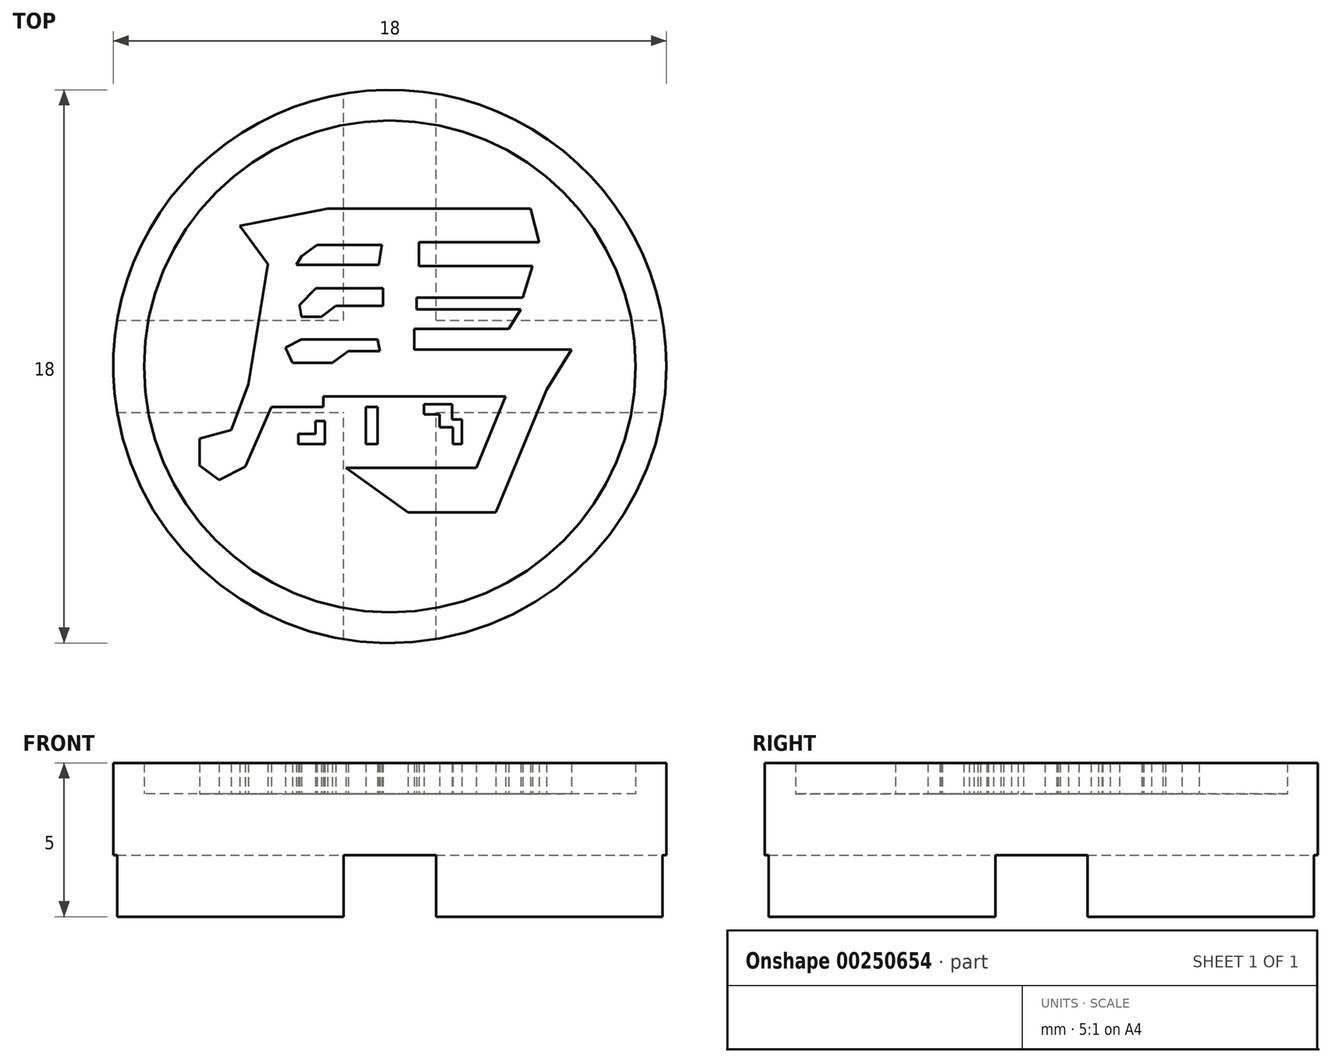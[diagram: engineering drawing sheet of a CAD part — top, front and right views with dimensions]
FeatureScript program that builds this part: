
annotation { "Feature Type Name" : "Feature", "Feature Type Description" : "" }
export const myFeature = defineFeature(function(context is Context, id is Id, definition is map)
    precondition{}
    {
        {
            var Q0;
            Q0=qCreatedBy(makeId("Top.planeOp"),FACE);
            var sketch = newSketch(context, id + "F0", { "sketchPlane" : qUnion([Q0])});
            skCircle(sketch, "E0", {"center": v(-31.33, 19.76) * mm, "radius": 9 * mm});
            skSolve(sketch);
        }
        {
            var Q0;
            Q0=qSketchRegion(id+"F0",true);
            extrude(context, id + "F1", {"entities" : qUnion([Q0]), "depth" : 4 * mm});
        }
        {
            var Q0;
            Q0=makeQuery(id+"F1.opExtrude","CAP_FACE",FACE,{"disambiguationData":[OSD([sQuery(id+"F0.wireOp",EDGE,"E0")])],"isStart":true});
            var sketch = newSketch(context, id + "F2", { "sketchPlane" : qUnion([Q0])});
            skLineSegment(sketch, "E1", {"start": v(-31.33, -19.76) * mm, "end": v(-22.33, -19.76) * mm, "construction": true});
            skLineSegment(sketch, "E2", {"start": v(-31.33, -19.76) * mm, "end": v(-31.33, -10.76) * mm, "construction": true});
            skLineSegment(sketch, "E3", {"start": v(-31.33, -19.76) * mm, "end": v(-40.33, -19.76) * mm, "construction": true});
            skLineSegment(sketch, "E4", {"start": v(-31.33, -19.76) * mm, "end": v(-31.33, -28.76) * mm, "construction": true});
            skLineSegment(sketch, "E5.bottom", {"start": v(-40.33, -28.76) * mm, "end": v(-22.33, -28.76) * mm});
            skLineSegment(sketch, "E5.top", {"start": v(-40.33, -10.76) * mm, "end": v(-22.33, -10.76) * mm});
            skLineSegment(sketch, "E5.left", {"start": v(-22.33, -10.76) * mm, "end": v(-22.33, -28.76) * mm});
            skLineSegment(sketch, "E5.right", {"start": v(-40.33, -10.76) * mm, "end": v(-40.33, -28.76) * mm});
            skPoint(sketch, "E6", {"position": v(-31.33, -28.76) * mm});
            skPoint(sketch, "E7", {"position": v(-40.33, -19.76) * mm});
            skPoint(sketch, "E8", {"position": v(-22.33, -19.76) * mm});
            skPoint(sketch, "E9", {"position": v(-31.33, -10.76) * mm});
            skLineSegment(sketch, "E10.bottom", {"start": v(-32.83, -10.76) * mm, "end": v(-29.83, -10.76) * mm});
            skLineSegment(sketch, "E10.top", {"start": v(-32.83, -28.76) * mm, "end": v(-29.83, -28.76) * mm});
            skLineSegment(sketch, "E10.left", {"start": v(-32.83, -10.76) * mm, "end": v(-32.83, -28.76) * mm});
            skLineSegment(sketch, "E10.right", {"start": v(-29.83, -10.76) * mm, "end": v(-29.83, -28.76) * mm});
            skLineSegment(sketch, "E11.bottom", {"start": v(-40.33, -18.26) * mm, "end": v(-22.33, -18.26) * mm});
            skLineSegment(sketch, "E11.top", {"start": v(-40.33, -21.26) * mm, "end": v(-22.33, -21.26) * mm});
            skLineSegment(sketch, "E11.left", {"start": v(-40.33, -18.26) * mm, "end": v(-40.33, -21.26) * mm});
            skLineSegment(sketch, "E11.right", {"start": v(-22.33, -18.26) * mm, "end": v(-22.33, -21.26) * mm});
            skSolve(sketch);
        }
        {
            var Q0;
            {var subQ1=sQuery(id+"F2.wireOp",EDGE,"E10.bottom");var subQ3=makeQuery(id+"F1.opExtrude","CAP_EDGE",EDGE,{"disambiguationData":[OSD([sQuery(id+"F0.wireOp",EDGE,"E0")])],"isStart":true});var subQ4=makeQuery(id+"F2.imprint","INTERSECT",VERTEX,{"derivedFrom":[subQ3,subQ1]});Q0=makeQuery(id+"F2.imprint","IMPRINT",FACE,{"disambiguationData":[TD([[makeQuery(id+"F2.imprint","IMPRINT",EDGE,{"disambiguationData":[TD([[subQ4,1.0]])],"derivedFrom":subQ3}),1.0]])]});}
            var Q1;
            {var subQ1=sQuery(id+"F2.wireOp",EDGE,"E10.bottom");var subQ3=makeQuery(id+"F1.opExtrude","CAP_EDGE",EDGE,{"disambiguationData":[OSD([sQuery(id+"F0.wireOp",EDGE,"E0")])],"isStart":true});var subQ4=makeQuery(id+"F2.imprint","INTERSECT",VERTEX,{"derivedFrom":[subQ3,subQ1]});Q1=makeQuery(id+"F2.imprint","IMPRINT",FACE,{"disambiguationData":[TD([[makeQuery(id+"F2.imprint","IMPRINT",EDGE,{"disambiguationData":[TD([[subQ4,-1.0]])],"derivedFrom":subQ3}),1.0]])]});}
            var Q2;
            {var subQ1=sQuery(id+"F2.wireOp",EDGE,"E10.top");var subQ3=makeQuery(id+"F1.opExtrude","CAP_EDGE",EDGE,{"disambiguationData":[OSD([sQuery(id+"F0.wireOp",EDGE,"E0")])],"isStart":true});var subQ4=makeQuery(id+"F2.imprint","INTERSECT",VERTEX,{"derivedFrom":[subQ3,subQ1]});Q2=makeQuery(id+"F2.imprint","IMPRINT",FACE,{"disambiguationData":[TD([[makeQuery(id+"F2.imprint","IMPRINT",EDGE,{"disambiguationData":[TD([[subQ4,-1.0]])],"derivedFrom":subQ3}),1.0]])]});}
            var Q3;
            {var subQ1=sQuery(id+"F2.wireOp",EDGE,"E10.top");var subQ3=makeQuery(id+"F1.opExtrude","CAP_EDGE",EDGE,{"disambiguationData":[OSD([sQuery(id+"F0.wireOp",EDGE,"E0")])],"isStart":true});var subQ4=makeQuery(id+"F2.imprint","INTERSECT",VERTEX,{"derivedFrom":[subQ3,subQ1]});Q3=makeQuery(id+"F2.imprint","IMPRINT",FACE,{"disambiguationData":[TD([[makeQuery(id+"F2.imprint","IMPRINT",EDGE,{"disambiguationData":[TD([[subQ4,1.0]])],"derivedFrom":subQ3}),1.0]])]});}
            var Q4;
            {var subQ0=sQuery(id+"F2.wireOp",EDGE,"E11.left");var subQ3=makeQuery(id+"F1.opExtrude","CAP_EDGE",EDGE,{"disambiguationData":[OSD([sQuery(id+"F0.wireOp",EDGE,"E0")])],"isStart":true});var subQ5=makeQuery(id+"F2.imprint","INTERSECT",VERTEX,{"derivedFrom":[subQ3,subQ0]});Q4=makeQuery(id+"F2.imprint","IMPRINT",FACE,{"disambiguationData":[TD([[makeQuery(id+"F2.imprint","IMPRINT",EDGE,{"disambiguationData":[TD([[subQ5,-1.0]])],"derivedFrom":subQ3}),1.0]])]});}
            var Q5;
            {var subQ0=sQuery(id+"F2.wireOp",EDGE,"E11.right");var subQ3=makeQuery(id+"F1.opExtrude","CAP_EDGE",EDGE,{"disambiguationData":[OSD([sQuery(id+"F0.wireOp",EDGE,"E0")])],"isStart":true});var subQ5=makeQuery(id+"F2.imprint","INTERSECT",VERTEX,{"derivedFrom":[subQ3,subQ0]});Q5=makeQuery(id+"F2.imprint","IMPRINT",FACE,{"disambiguationData":[TD([[makeQuery(id+"F2.imprint","IMPRINT",EDGE,{"disambiguationData":[TD([[subQ5,1.0]])],"derivedFrom":subQ3}),1.0]])]});}
            var Q6;
            {var subQ0=sQuery(id+"F2.wireOp",EDGE,"E11.left");var subQ3=makeQuery(id+"F1.opExtrude","CAP_EDGE",EDGE,{"disambiguationData":[OSD([sQuery(id+"F0.wireOp",EDGE,"E0")])],"isStart":true});var subQ5=makeQuery(id+"F2.imprint","INTERSECT",VERTEX,{"derivedFrom":[subQ3,subQ0]});Q6=makeQuery(id+"F2.imprint","IMPRINT",FACE,{"disambiguationData":[TD([[makeQuery(id+"F2.imprint","IMPRINT",EDGE,{"disambiguationData":[TD([[subQ5,1.0]])],"derivedFrom":subQ3}),1.0]])]});}
            var Q7;
            {var subQ0=sQuery(id+"F2.wireOp",EDGE,"E11.right");var subQ3=makeQuery(id+"F1.opExtrude","CAP_EDGE",EDGE,{"disambiguationData":[OSD([sQuery(id+"F0.wireOp",EDGE,"E0")])],"isStart":true});var subQ5=makeQuery(id+"F2.imprint","INTERSECT",VERTEX,{"derivedFrom":[subQ3,subQ0]});Q7=makeQuery(id+"F2.imprint","IMPRINT",FACE,{"disambiguationData":[TD([[makeQuery(id+"F2.imprint","IMPRINT",EDGE,{"disambiguationData":[TD([[subQ5,-1.0]])],"derivedFrom":subQ3}),1.0]])]});}
            var Q8;
            {var subQ3=makeQuery(id+"F1.opExtrude","CAP_EDGE",EDGE,{"disambiguationData":[OSD([sQuery(id+"F0.wireOp",EDGE,"E0")])],"isStart":true});var subQ5=sQuery(id+"F2.wireOp",EDGE,"E10.left");var subQ8=makeQuery(id+"F2.imprint","INTERSECT",VERTEX,{"disambiguationData":[OD(1.0)],"derivedFrom":[subQ3,subQ5]});Q8=makeQuery(id+"F2.imprint","IMPRINT",FACE,{"disambiguationData":[TD([[makeQuery(id+"F2.imprint","IMPRINT",EDGE,{"disambiguationData":[TD([[subQ8,-1.0]])],"derivedFrom":subQ3}),1.0]])]});}
            var Q9;
            {var subQ3=makeQuery(id+"F1.opExtrude","CAP_EDGE",EDGE,{"disambiguationData":[OSD([sQuery(id+"F0.wireOp",EDGE,"E0")])],"isStart":true});var subQ5=sQuery(id+"F2.wireOp",EDGE,"E10.right");var subQ8=makeQuery(id+"F2.imprint","INTERSECT",VERTEX,{"disambiguationData":[OD(1.0)],"derivedFrom":[subQ3,subQ5]});Q9=makeQuery(id+"F2.imprint","IMPRINT",FACE,{"disambiguationData":[TD([[makeQuery(id+"F2.imprint","IMPRINT",EDGE,{"disambiguationData":[TD([[subQ8,1.0]])],"derivedFrom":subQ3}),1.0]])]});}
            var Q10;
            {var subQ3=makeQuery(id+"F1.opExtrude","CAP_EDGE",EDGE,{"disambiguationData":[OSD([sQuery(id+"F0.wireOp",EDGE,"E0")])],"isStart":true});var subQ5=sQuery(id+"F2.wireOp",EDGE,"E10.left");var subQ8=makeQuery(id+"F2.imprint","INTERSECT",VERTEX,{"disambiguationData":[OD(0.0)],"derivedFrom":[subQ3,subQ5]});Q10=makeQuery(id+"F2.imprint","IMPRINT",FACE,{"disambiguationData":[TD([[makeQuery(id+"F2.imprint","IMPRINT",EDGE,{"disambiguationData":[TD([[subQ8,1.0]])],"derivedFrom":subQ3}),1.0]])]});}
            var Q11;
            {var subQ3=makeQuery(id+"F1.opExtrude","CAP_EDGE",EDGE,{"disambiguationData":[OSD([sQuery(id+"F0.wireOp",EDGE,"E0")])],"isStart":true});var subQ5=sQuery(id+"F2.wireOp",EDGE,"E10.right");var subQ8=makeQuery(id+"F2.imprint","INTERSECT",VERTEX,{"disambiguationData":[OD(0.0)],"derivedFrom":[subQ3,subQ5]});Q11=makeQuery(id+"F2.imprint","IMPRINT",FACE,{"disambiguationData":[TD([[makeQuery(id+"F2.imprint","IMPRINT",EDGE,{"disambiguationData":[TD([[subQ8,-1.0]])],"derivedFrom":subQ3}),1.0]])]});}
            var Q12;
            {var subQ2=sQuery(id+"F2.wireOp",EDGE,"E10.left");var subQ4=sQuery(id+"F2.wireOp",EDGE,"E11.bottom");var subQ8=makeQuery(id+"F2.imprint","INTERSECT",VERTEX,{"derivedFrom":[subQ2,subQ4]});Q12=makeQuery(id+"F2.imprint","IMPRINT",FACE,{"disambiguationData":[TD([[makeQuery(id+"F2.imprint","IMPRINT",EDGE,{"disambiguationData":[TD([[subQ8,1.0]])],"derivedFrom":subQ2}),1.0]])]});}
            var Q13;
            {var subQ1=sQuery(id+"F2.wireOp",EDGE,"E10.left");var subQ5=sQuery(id+"F2.wireOp",EDGE,"E11.bottom");var subQ6=makeQuery(id+"F2.imprint","INTERSECT",VERTEX,{"derivedFrom":[subQ1,subQ5]});Q13=makeQuery(id+"F2.imprint","IMPRINT",FACE,{"disambiguationData":[TD([[makeQuery(id+"F2.imprint","IMPRINT",EDGE,{"disambiguationData":[TD([[subQ6,-1.0]])],"derivedFrom":subQ1}),-1.0]])]});}
            var Q14;
            {var subQ0=sQuery(id+"F2.wireOp",EDGE,"E11.top");var subQ1=sQuery(id+"F2.wireOp",EDGE,"E10.left");var subQ2=makeQuery(id+"F2.imprint","INTERSECT",VERTEX,{"derivedFrom":[subQ1,subQ0]});Q14=makeQuery(id+"F2.imprint","IMPRINT",FACE,{"disambiguationData":[TD([[makeQuery(id+"F2.imprint","IMPRINT",EDGE,{"disambiguationData":[TD([[subQ2,-1.0]])],"derivedFrom":subQ1}),1.0]])]});}
            var Q15;
            {var subQ2=sQuery(id+"F2.wireOp",EDGE,"E11.bottom");var subQ5=sQuery(id+"F2.wireOp",EDGE,"E10.right");var subQ8=makeQuery(id+"F2.imprint","INTERSECT",VERTEX,{"derivedFrom":[subQ5,subQ2]});Q15=makeQuery(id+"F2.imprint","IMPRINT",FACE,{"disambiguationData":[TD([[makeQuery(id+"F2.imprint","IMPRINT",EDGE,{"disambiguationData":[TD([[subQ8,-1.0]])],"derivedFrom":subQ5}),1.0]])]});}
            var Q16;
            {var subQ0=sQuery(id+"F2.wireOp",EDGE,"E11.bottom");var subQ1=sQuery(id+"F2.wireOp",EDGE,"E10.left");var subQ2=makeQuery(id+"F2.imprint","INTERSECT",VERTEX,{"derivedFrom":[subQ1,subQ0]});Q16=makeQuery(id+"F2.imprint","IMPRINT",FACE,{"disambiguationData":[TD([[makeQuery(id+"F2.imprint","IMPRINT",EDGE,{"disambiguationData":[TD([[subQ2,-1.0]])],"derivedFrom":subQ1}),1.0]])]});}
            extrude(context, id + "F3", {"entities" : qUnion([Q0, Q1, Q2, Q3, Q4, Q5, Q6, Q7, Q8, Q9, Q10, Q11, Q12, Q13, Q14, Q15, Q16]), "operationType" : NewBodyOperationType.REMOVE, "oppositeDirection" : true, "depth" : 2 * mm});
        }
        {
            var Q0;
            Q0=makeQuery(id+"F1.opExtrude","CAP_FACE",FACE,{"disambiguationData":[OSD([sQuery(id+"F0.wireOp",EDGE,"E0")])],"isStart":false});
            var sketch = newSketch(context, id + "F5", { "sketchPlane" : qUnion([Q0])});
            skCircle(sketch, "E12", {"center": v(-31.33, 19.76) * mm, "radius": 9 * mm});
            skPoint(sketch, "E12.first.point", {"position": v(-33.38, 11) * mm});
            skPoint(sketch, "E12.second.point", {"position": v(-27.6, 27.94) * mm});
            skPoint(sketch, "E12.third.point", {"position": v(-40.33, 19.54) * mm});
            skCircle(sketch, "E13", {"center": v(-31.33, 19.76) * mm, "radius": 8 * mm});
            skLineSegment(sketch, "E14", {"start": v(-36.21, 24.33) * mm, "end": v(-33.35, 24.9) * mm});
            skLineSegment(sketch, "E15", {"start": v(-33.35, 24.9) * mm, "end": v(-26.76, 24.9) * mm});
            skLineSegment(sketch, "E16", {"start": v(-26.76, 24.9) * mm, "end": v(-26.47, 23.8) * mm});
            skLineSegment(sketch, "E17", {"start": v(-26.47, 23.8) * mm, "end": v(-30.4, 23.8) * mm});
            skLineSegment(sketch, "E18", {"start": v(-30.4, 23.8) * mm, "end": v(-30.4, 23.02) * mm});
            skLineSegment(sketch, "E19", {"start": v(-30.4, 23.02) * mm, "end": v(-26.69, 23.02) * mm});
            skLineSegment(sketch, "E20", {"start": v(-26.69, 23.02) * mm, "end": v(-27, 22) * mm});
            skLineSegment(sketch, "E21", {"start": v(-27, 22) * mm, "end": v(-30.46, 22) * mm});
            skLineSegment(sketch, "E22", {"start": v(-30.46, 22) * mm, "end": v(-30.46, 21.61) * mm});
            skLineSegment(sketch, "E23", {"start": v(-30.46, 21.61) * mm, "end": v(-27.07, 21.61) * mm});
            skLineSegment(sketch, "E24", {"start": v(-27.07, 21.61) * mm, "end": v(-27.46, 20.98) * mm});
            skLineSegment(sketch, "E25", {"start": v(-27.46, 20.98) * mm, "end": v(-30.53, 20.98) * mm});
            skLineSegment(sketch, "E26", {"start": v(-30.53, 20.98) * mm, "end": v(-30.53, 20.3) * mm});
            skLineSegment(sketch, "E27", {"start": v(-30.53, 20.3) * mm, "end": v(-25.42, 20.3) * mm});
            skLineSegment(sketch, "E28", {"start": v(-25.42, 20.3) * mm, "end": v(-26.23, 19) * mm});
            skLineSegment(sketch, "E29", {"start": v(-26.23, 19) * mm, "end": v(-27.89, 15.01) * mm});
            skLineSegment(sketch, "E30", {"start": v(-27.89, 15.01) * mm, "end": v(-30.74, 15.01) * mm});
            skLineSegment(sketch, "E31", {"start": v(-30.74, 15.01) * mm, "end": v(-32.75, 16.46) * mm});
            skLineSegment(sketch, "E32", {"start": v(-32.75, 16.46) * mm, "end": v(-28.52, 16.46) * mm});
            skLineSegment(sketch, "E33", {"start": v(-28.52, 16.46) * mm, "end": v(-27.57, 18.79) * mm});
            skLineSegment(sketch, "E34", {"start": v(-27.57, 18.79) * mm, "end": v(-33.5, 18.79) * mm});
            skLineSegment(sketch, "E35", {"start": v(-33.5, 18.79) * mm, "end": v(-33.5, 18.44) * mm});
            skLineSegment(sketch, "E36", {"start": v(-33.5, 18.44) * mm, "end": v(-35.19, 18.44) * mm});
            skLineSegment(sketch, "E37", {"start": v(-35.19, 18.44) * mm, "end": v(-36.04, 16.5) * mm});
            skLineSegment(sketch, "E38", {"start": v(-36.04, 16.5) * mm, "end": v(-36.88, 16.07) * mm});
            skLineSegment(sketch, "E39", {"start": v(-36.88, 16.07) * mm, "end": v(-37.52, 16.53) * mm});
            skLineSegment(sketch, "E40", {"start": v(-37.52, 16.53) * mm, "end": v(-37.52, 17.41) * mm});
            skLineSegment(sketch, "E41", {"start": v(-37.52, 17.41) * mm, "end": v(-36.5, 17.7) * mm});
            skLineSegment(sketch, "E42", {"start": v(-36.5, 17.7) * mm, "end": v(-35.93, 19.18) * mm});
            skLineSegment(sketch, "E43", {"start": v(-35.93, 19.18) * mm, "end": v(-35.3, 23.1) * mm});
            skLineSegment(sketch, "E44", {"start": v(-35.3, 23.1) * mm, "end": v(-36.21, 24.33) * mm});
            skLineSegment(sketch, "E45", {"start": v(-34.2, 23.34) * mm, "end": v(-33.7, 23.71) * mm});
            skPoint(sketch, "E45.endSnap0", {"position": v(-35.75, 23.71) * mm});
            skLineSegment(sketch, "E46", {"start": v(-33.7, 23.71) * mm, "end": v(-31.59, 23.71) * mm});
            skLineSegment(sketch, "E47", {"start": v(-31.59, 23.71) * mm, "end": v(-31.7, 23.06) * mm});
            skLineSegment(sketch, "E48", {"start": v(-31.7, 23.06) * mm, "end": v(-34.38, 23.06) * mm});
            skLineSegment(sketch, "E49", {"start": v(-34.38, 23.06) * mm, "end": v(-34.2, 23.34) * mm});
            skLineSegment(sketch, "E50", {"start": v(-34.73, 20.38) * mm, "end": v(-34.5, 19.87) * mm});
            skLineSegment(sketch, "E51", {"start": v(-34.5, 19.87) * mm, "end": v(-33.2, 19.87) * mm});
            skLineSegment(sketch, "E52", {"start": v(-33.2, 19.87) * mm, "end": v(-32.69, 20.26) * mm});
            skLineSegment(sketch, "E53", {"start": v(-32.69, 20.26) * mm, "end": v(-31.65, 20.26) * mm});
            skLineSegment(sketch, "E54", {"start": v(-31.65, 20.26) * mm, "end": v(-31.73, 20.64) * mm});
            skLineSegment(sketch, "E55", {"start": v(-31.73, 20.64) * mm, "end": v(-34.2, 20.64) * mm});
            skLineSegment(sketch, "E56", {"start": v(-34.2, 20.64) * mm, "end": v(-34.73, 20.38) * mm});
            skLineSegment(sketch, "E57", {"start": v(-33.74, 22.3) * mm, "end": v(-31.55, 22.3) * mm});
            skLineSegment(sketch, "E58", {"start": v(-31.55, 22.3) * mm, "end": v(-31.55, 21.73) * mm});
            skLineSegment(sketch, "E59", {"start": v(-31.55, 21.73) * mm, "end": v(-33.1, 21.73) * mm});
            skLineSegment(sketch, "E60", {"start": v(-33.1, 21.73) * mm, "end": v(-33.56, 21.37) * mm});
            skLineSegment(sketch, "E61", {"start": v(-33.56, 21.37) * mm, "end": v(-34.2, 21.37) * mm});
            skLineSegment(sketch, "E62", {"start": v(-34.2, 21.37) * mm, "end": v(-34.28, 21.75) * mm});
            skLineSegment(sketch, "E63", {"start": v(-34.28, 21.75) * mm, "end": v(-33.74, 22.3) * mm});
            skLineSegment(sketch, "E64", {"start": v(-34.3, 17.57) * mm, "end": v(-34.3, 17.23) * mm});
            skLineSegment(sketch, "E65", {"start": v(-34.3, 17.23) * mm, "end": v(-33.45, 17.23) * mm});
            skLineSegment(sketch, "E66", {"start": v(-33.45, 17.23) * mm, "end": v(-33.45, 17.98) * mm});
            skLineSegment(sketch, "E67", {"start": v(-33.45, 17.98) * mm, "end": v(-33.74, 17.98) * mm});
            skLineSegment(sketch, "E68", {"start": v(-33.74, 17.98) * mm, "end": v(-33.74, 17.57) * mm});
            skLineSegment(sketch, "E69", {"start": v(-33.74, 17.57) * mm, "end": v(-34.3, 17.57) * mm});
            skLineSegment(sketch, "E70", {"start": v(-32.1, 18.44) * mm, "end": v(-32.1, 17.23) * mm});
            skLineSegment(sketch, "E71", {"start": v(-32.1, 17.23) * mm, "end": v(-31.74, 17.23) * mm});
            skLineSegment(sketch, "E72", {"start": v(-31.74, 17.23) * mm, "end": v(-31.74, 18.44) * mm});
            skLineSegment(sketch, "E73", {"start": v(-31.74, 18.44) * mm, "end": v(-32.1, 18.44) * mm});
            skLineSegment(sketch, "E74", {"start": v(-30.22, 18.53) * mm, "end": v(-30.22, 18.2) * mm});
            skLineSegment(sketch, "E75", {"start": v(-30.22, 18.2) * mm, "end": v(-29.7, 18.2) * mm});
            skLineSegment(sketch, "E76", {"start": v(-29.7, 18.2) * mm, "end": v(-29.7, 17.78) * mm});
            skLineSegment(sketch, "E77", {"start": v(-29.7, 17.78) * mm, "end": v(-29.28, 17.78) * mm});
            skLineSegment(sketch, "E78", {"start": v(-29.28, 17.78) * mm, "end": v(-29.28, 17.23) * mm});
            skLineSegment(sketch, "E79", {"start": v(-29.28, 17.23) * mm, "end": v(-28.98, 17.23) * mm});
            skLineSegment(sketch, "E80", {"start": v(-28.98, 17.23) * mm, "end": v(-28.98, 18.03) * mm});
            skLineSegment(sketch, "E81", {"start": v(-28.98, 18.03) * mm, "end": v(-29.31, 18.03) * mm});
            skLineSegment(sketch, "E82", {"start": v(-30.22, 18.53) * mm, "end": v(-29.31, 18.53) * mm});
            skLineSegment(sketch, "E83", {"start": v(-29.31, 18.53) * mm, "end": v(-29.31, 18.03) * mm});
            skSolve(sketch);
        }
        {
            var Q0;
            Q0 = qSketchRegion(id + "F5", true);
            var Q1;
            Q1=makeQuery(id+"F5.imprint","IMPRINT",FACE,{"disambiguationData":[TD([[makeQuery(id+"F5.imprint","IMPRINT",EDGE,{"derivedFrom":sQuery(id+"F5.wireOp",EDGE,"E14")}),-1.0]])]});
            var Q2;
            Q2=makeQuery(id+"F5.imprint","IMPRINT",FACE,{"disambiguationData":[TD([[makeQuery(id+"F5.imprint","IMPRINT",EDGE,{"derivedFrom":sQuery(id+"F5.wireOp",EDGE,"E64")}),1.0]])]});
            var Q3;
            Q3=makeQuery(id+"F5.imprint","IMPRINT",FACE,{"disambiguationData":[TD([[makeQuery(id+"F5.imprint","IMPRINT",EDGE,{"derivedFrom":sQuery(id+"F5.wireOp",EDGE,"E70")}),1.0]])]});
            var Q4;
            Q4=makeQuery(id+"F5.imprint","IMPRINT",FACE,{"disambiguationData":[TD([[makeQuery(id+"F5.imprint","IMPRINT",EDGE,{"derivedFrom":sQuery(id+"F5.wireOp",EDGE,"E74")}),1.0]])]});
            extrude(context, id + "F4", {"entities" : qUnion([Q0, Q1, Q2, Q3, Q4]), "operationType" : NewBodyOperationType.ADD, "depth" : 1 * mm});
        }
    });
